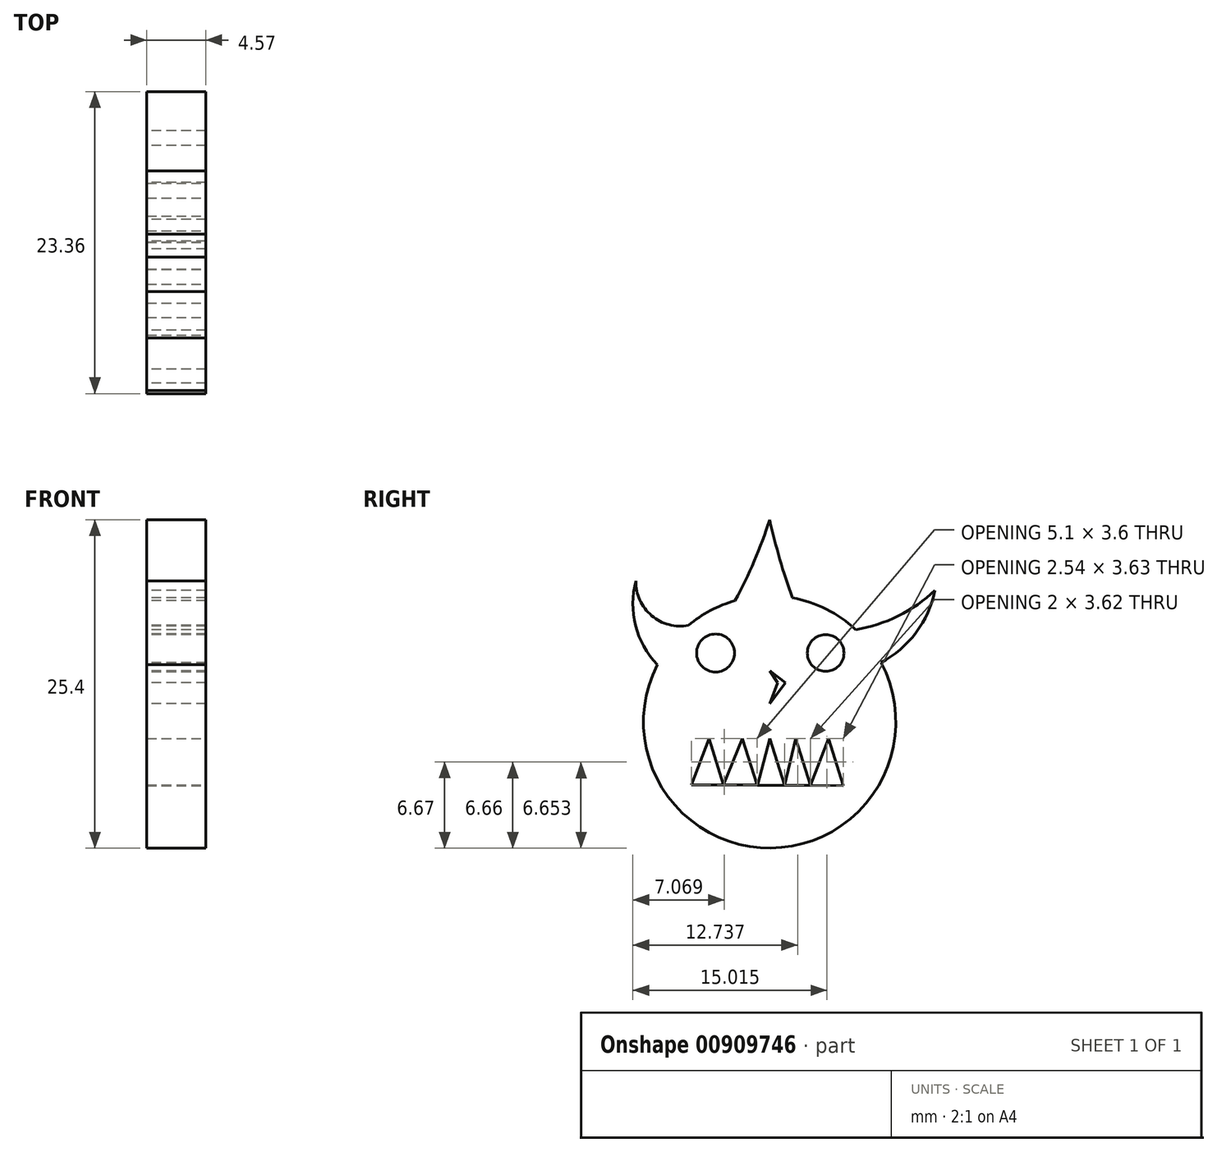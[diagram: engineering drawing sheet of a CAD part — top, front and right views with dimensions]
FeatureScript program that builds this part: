
annotation { "Feature Type Name" : "Feature", "Feature Type Description" : "" }
export const myFeature = defineFeature(function(context is Context, id is Id, definition is map)
    precondition{}
    {
        {
            var Q0;
            Q0=qCreatedBy(makeId("Right.planeOp"),FACE);
            var sketch = newSketch(context, id + "F0", { "sketchPlane" : qUnion([Q0])});
            skCircle(sketch, "E0", {"center": v(0, 0) * mm, "radius": 9.76 * mm});
            skCircle(sketch, "E1", {"center": v(-4.18, 5.33) * mm, "radius": 1.47 * mm});
            skCircle(sketch, "E2", {"center": v(4.33, 5.33) * mm, "radius": 1.42 * mm});
            skArc(sketch, "E3", {"start": v(-10.34, 10.91) * mm, "mid": v(-10.38, 7.45) * mm, "end": v(-8.7, 4.43) * mm});
            skArc(sketch, "E4", {"start": v(-10.34, 10.91) * mm, "mid": v(-9.13, 8.22) * mm, "end": v(-6.28, 7.47) * mm});
            skArc(sketch, "E5", {"start": v(8.61, 4.59) * mm, "mid": v(11.33, 6.92) * mm, "end": v(12.78, 10.18) * mm});
            skArc(sketch, "E6", {"start": v(6.65, 7.14) * mm, "mid": v(9.95, 8.2) * mm, "end": v(12.78, 10.18) * mm});
            skArc(sketch, "E7", {"start": v(-2.68, 9.38) * mm, "mid": v(-1.2, 12.45) * mm, "end": v(0, 15.64) * mm});
            skArc(sketch, "E8", {"start": v(0, 15.64) * mm, "mid": v(0.79, 12.6) * mm, "end": v(1.76, 9.6) * mm});
            skLineSegment(sketch, "E9", {"start": v(0, 3.97) * mm, "end": v(1.23, 3.02) * mm});
            skLineSegment(sketch, "E10", {"start": v(1.23, 3.02) * mm, "end": v(0, 1.43) * mm});
            skLineSegment(sketch, "E11", {"start": v(0, 1.43) * mm, "end": v(0.61, 3.02) * mm});
            skPoint(sketch, "E11.endSnap0", {"position": v(0.61, 2.22) * mm});
            skLineSegment(sketch, "E12", {"start": v(0.61, 3.02) * mm, "end": v(0, 3.97) * mm});
            skSolve(sketch);
        }
        {
            var Q0;
            Q0=makeQuery(id+"F0.imprint","IMPRINT",FACE,{"disambiguationData":[TD([[makeQuery(id+"F0.imprint","IMPRINT",EDGE,{"derivedFrom":sQuery(id+"F0.wireOp",EDGE,"E0")}),1.0]])]});
            var Q1;
            {var subQ0=sQuery(id+"F0.wireOp",EDGE,"E3");Q1=makeQuery(id+"F0.imprint","IMPRINT",FACE,{"disambiguationData":[TD([[makeQuery(id+"F0.imprint","IMPRINT",EDGE,{"derivedFrom":subQ0}),1.0]])]});}
            var Q2;
            {var subQ0=sQuery(id+"F0.wireOp",EDGE,"E7");Q2=makeQuery(id+"F0.imprint","IMPRINT",FACE,{"disambiguationData":[TD([[makeQuery(id+"F0.imprint","IMPRINT",EDGE,{"derivedFrom":subQ0}),-1.0]])]});}
            var Q3;
            {var subQ0=sQuery(id+"F0.wireOp",EDGE,"E5");Q3=makeQuery(id+"F0.imprint","IMPRINT",FACE,{"disambiguationData":[TD([[makeQuery(id+"F0.imprint","IMPRINT",EDGE,{"derivedFrom":subQ0}),1.0]])]});}
            extrude(context, id + "F1", {"entities" : qUnion([Q0, Q1, Q2, Q3]), "depth" : 4.57 * mm, "offsetDistance" : 25.4 * mm});
        }
        {
            var Q0;
            Q0=makeQuery(id+"F1.opExtrude","CAP_FACE",FACE,{"disambiguationData":[OSD([sQuery(id+"F0.wireOp",EDGE,"E0"),sQuery(id+"F0.wireOp",EDGE,"E1"),sQuery(id+"F0.wireOp",EDGE,"E2")])],"isStart":false});
            var sketch = newSketch(context, id + "F2", { "sketchPlane" : qUnion([Q0])});
            skLineSegment(sketch, "E13", {"start": v(-3.56, -4.86) * mm, "end": v(-2.1, -1.3) * mm});
            skLineSegment(sketch, "E14", {"start": v(-2.1, -1.3) * mm, "end": v(-0.95, -4.92) * mm});
            skLineSegment(sketch, "E15", {"start": v(-0.95, -4.92) * mm, "end": v(0, -1.3) * mm});
            skLineSegment(sketch, "E16", {"start": v(0, -1.3) * mm, "end": v(1.15, -4.92) * mm});
            skLineSegment(sketch, "E17", {"start": v(1.15, -4.92) * mm, "end": v(2.01, -1.3) * mm});
            skLineSegment(sketch, "E18", {"start": v(2.01, -1.3) * mm, "end": v(3.16, -4.92) * mm});
            skLineSegment(sketch, "E19", {"start": v(3.16, -4.92) * mm, "end": v(4.55, -1.3) * mm});
            skLineSegment(sketch, "E20", {"start": v(4.55, -1.3) * mm, "end": v(5.7, -4.92) * mm});
            skLineSegment(sketch, "E21", {"start": v(-3.56, -4.86) * mm, "end": v(-4.7, -1.3) * mm});
            skLineSegment(sketch, "E22", {"start": v(-4.7, -1.3) * mm, "end": v(-6.06, -4.86) * mm});
            skLineSegment(sketch, "E23", {"start": v(-6.06, -4.86) * mm, "end": v(5.7, -4.92) * mm});
            skSolve(sketch);
        }
        {
            var Q0;
            {var subQ1=sQuery(id+"F2.wireOp",EDGE,"E13");Q0=makeQuery(id+"F2.imprint","IMPRINT",FACE,{"disambiguationData":[TD([[makeQuery(id+"F2.imprint","IMPRINT",EDGE,{"derivedFrom":subQ1}),-1.0]])]});}
            var Q1;
            {var subQ0=sQuery(id+"F2.wireOp",EDGE,"E16");var subQ1=sQuery(id+"F2.wireOp",EDGE,"E15");var subQ2=makeQuery(id+"F2.imprint","INTERSECT",VERTEX,{"derivedFrom":[subQ1,subQ0]});Q1=makeQuery(id+"F2.imprint","IMPRINT",FACE,{"disambiguationData":[TD([[makeQuery(id+"F2.imprint","IMPRINT",EDGE,{"disambiguationData":[TD([[subQ2,1.0]])],"derivedFrom":subQ1}),-1.0]])]});}
            var Q2;
            {var subQ0=sQuery(id+"F2.wireOp",EDGE,"E18");var subQ1=sQuery(id+"F2.wireOp",EDGE,"E17");var subQ2=makeQuery(id+"F2.imprint","INTERSECT",VERTEX,{"derivedFrom":[subQ1,subQ0]});Q2=makeQuery(id+"F2.imprint","IMPRINT",FACE,{"disambiguationData":[TD([[makeQuery(id+"F2.imprint","IMPRINT",EDGE,{"disambiguationData":[TD([[subQ2,1.0]])],"derivedFrom":subQ1}),-1.0]])]});}
            var Q3;
            {var subQ0=sQuery(id+"F2.wireOp",EDGE,"E20");Q3=makeQuery(id+"F2.imprint","IMPRINT",FACE,{"disambiguationData":[TD([[makeQuery(id+"F2.imprint","IMPRINT",EDGE,{"derivedFrom":subQ0}),-1.0]])]});}
            extrude(context, id + "F3", {"entities" : qUnion([Q0, Q1, Q2, Q3]), "operationType" : NewBodyOperationType.REMOVE, "oppositeDirection" : true, "depth" : 43.18 * mm, "offsetDistance" : 25.4 * mm});
        }
    });
